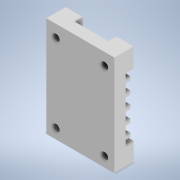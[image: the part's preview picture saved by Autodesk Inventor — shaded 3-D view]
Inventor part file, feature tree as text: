
AUTODESK INVENTOR PART (.ipt)
format: ipt  version: 2020 (Build 240168000, 168)  size: 249,344 bytes
history: native  units: in
note: dims shown in document units (in); Inventor stores cm internally (conversion verified against a paired STEP export)
features: extrude x5, sketch x5, other x3, reference x2, plane x1
ambient origin geometry x8: Origin, YZ Plane, XZ Plane, XY Plane, X Axis, Y Axis, Z Axis, Center Point
bodies: Solid1 (feature_tree)
feature tree (16):
  extrude  "Extrusion1"  Depth=0.21in
  extrude  "Extrusion2"  Depth=0.625in
  plane  "Work Plane1"
  extrude  "Extrusion3"  Depth=0.315in
  extrude  "Extrusion4"  Depth=0.125in
  extrude  "Extrusion5"  Depth=0.21in TaperAngle=0.0deg
  sketch  "Sketch1"  dims[d0=0.5in d1=0.0in d2=0.21in]
  reference  "Reference1"
  sketch  "Sketch2"  dims[d3=3.0in d4=0.0in d6=0.625in]
  sketch  "Sketch3"  dims[d7=0.1in d8=1.9685in d10=0.315in d11=0.3937in d13=1.0in]
  reference  "Reference4"
  sketch  "Sketch4"  dims[d15=0.21in d16=0.0in d17=0.125in]
  sketch  "Sketch5"  dims[d18=0.125in d19=0.21in d20=0.0in d21=0.0in d22=0.085in d23=0.0in d5=0.0344in]
  other  "<userpath>\Desktop\PnP Machine\PnP Machine.iam"
  other  "PnP Machine.iam"
  other  "Transmission Clamp:2"
